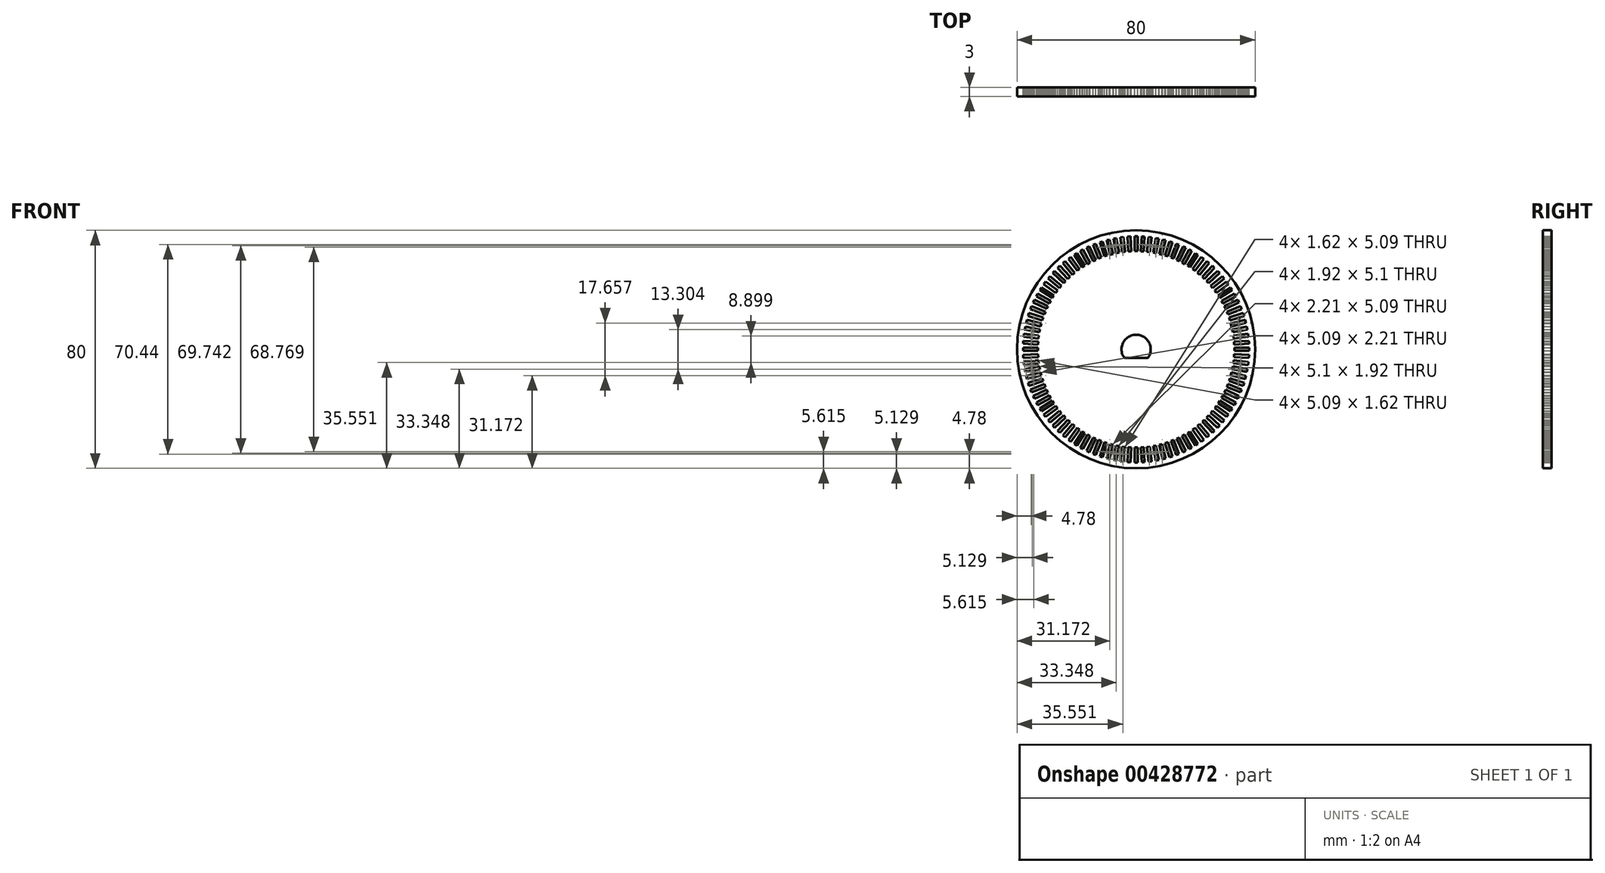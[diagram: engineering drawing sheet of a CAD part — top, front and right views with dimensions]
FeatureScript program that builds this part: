
annotation { "Feature Type Name" : "Feature", "Feature Type Description" : "" }
export const myFeature = defineFeature(function(context is Context, id is Id, definition is map)
    precondition{}
    {
        {
            var Q0;
            Q0=qCreatedBy(makeId("Front.planeOp"),FACE);
            var sketch = newSketch(context, id + "F0", { "sketchPlane" : qUnion([Q0])});
            skCircle(sketch, "E0", {"center": v(0, 0) * mm, "radius": 40 * mm});
            skLineSegment(sketch, "E1", {"start": v(0, 0) * mm, "end": v(0, 33) * mm});
            skLineSegment(sketch, "E2", {"start": v(0, 33) * mm, "end": v(0, 35.5) * mm});
            skLineSegment(sketch, "E3.bottom", {"start": v(0.5, 33) * mm, "end": v(-0.5, 33) * mm});
            skLineSegment(sketch, "E3.top", {"start": v(0.5, 38) * mm, "end": v(-0.5, 38) * mm});
            skLineSegment(sketch, "E3.left", {"start": v(0.5, 33) * mm, "end": v(0.5, 38) * mm});
            skLineSegment(sketch, "E3.right", {"start": v(-0.5, 33) * mm, "end": v(-0.5, 38) * mm});
            skPoint(sketch, "E3.middle", {"position": v(0, 35.5) * mm});
            skLineSegment(sketch, "E4.1.0", {"start": v(-2.57, 32.9) * mm, "end": v(-2.89, 37.9) * mm});
            skLineSegment(sketch, "E4.1.1", {"start": v(-1.57, 32.97) * mm, "end": v(-1.89, 37.96) * mm});
            skLineSegment(sketch, "E4.1.2", {"start": v(-2.07, 32.93) * mm, "end": v(-2.23, 35.43) * mm});
            skPoint(sketch, "E4.1.3", {"position": v(-2.23, 35.43) * mm});
            skLineSegment(sketch, "E4.1.4", {"start": v(-1.89, 37.96) * mm, "end": v(-2.89, 37.9) * mm});
            skLineSegment(sketch, "E4.1.5", {"start": v(-1.57, 32.97) * mm, "end": v(-2.57, 32.9) * mm});
            skLineSegment(sketch, "E4.2.0", {"start": v(-4.63, 32.68) * mm, "end": v(-5.26, 37.64) * mm});
            skLineSegment(sketch, "E4.2.1", {"start": v(-3.64, 32.8) * mm, "end": v(-4.27, 37.76) * mm});
            skLineSegment(sketch, "E4.2.2", {"start": v(-4.14, 32.74) * mm, "end": v(-4.45, 35.22) * mm});
            skPoint(sketch, "E4.2.3", {"position": v(-4.45, 35.22) * mm});
            skLineSegment(sketch, "E4.2.4", {"start": v(-4.27, 37.76) * mm, "end": v(-5.26, 37.64) * mm});
            skLineSegment(sketch, "E4.2.5", {"start": v(-3.64, 32.8) * mm, "end": v(-4.63, 32.68) * mm});
            skLineSegment(sketch, "E4.3.0", {"start": v(-6.67, 32.32) * mm, "end": v(-7.61, 37.23) * mm});
            skLineSegment(sketch, "E4.3.1", {"start": v(-5.7, 32.5) * mm, "end": v(-6.63, 37.42) * mm});
            skLineSegment(sketch, "E4.3.2", {"start": v(-6.18, 32.42) * mm, "end": v(-6.65, 34.87) * mm});
            skPoint(sketch, "E4.3.3", {"position": v(-6.65, 34.87) * mm});
            skLineSegment(sketch, "E4.3.4", {"start": v(-6.63, 37.42) * mm, "end": v(-7.61, 37.23) * mm});
            skLineSegment(sketch, "E4.3.5", {"start": v(-5.7, 32.5) * mm, "end": v(-6.67, 32.32) * mm});
            skLineSegment(sketch, "E4.4.0", {"start": v(-8.7, 31.84) * mm, "end": v(-9.93, 36.68) * mm});
            skLineSegment(sketch, "E4.4.1", {"start": v(-7.72, 32.09) * mm, "end": v(-8.97, 36.93) * mm});
            skLineSegment(sketch, "E4.4.2", {"start": v(-8.2, 31.96) * mm, "end": v(-8.83, 34.38) * mm});
            skPoint(sketch, "E4.4.3", {"position": v(-8.83, 34.38) * mm});
            skLineSegment(sketch, "E4.4.4", {"start": v(-8.97, 36.93) * mm, "end": v(-9.93, 36.68) * mm});
            skLineSegment(sketch, "E4.4.5", {"start": v(-7.72, 32.09) * mm, "end": v(-8.7, 31.84) * mm});
            skLineSegment(sketch, "E4.5.0", {"start": v(-10.67, 31.23) * mm, "end": v(-12.22, 35.99) * mm});
            skLineSegment(sketch, "E4.5.1", {"start": v(-9.72, 31.54) * mm, "end": v(-11.27, 36.3) * mm});
            skLineSegment(sketch, "E4.5.2", {"start": v(-10.2, 31.38) * mm, "end": v(-10.97, 33.76) * mm});
            skPoint(sketch, "E4.5.3", {"position": v(-10.97, 33.76) * mm});
            skLineSegment(sketch, "E4.5.4", {"start": v(-11.27, 36.3) * mm, "end": v(-12.22, 35.99) * mm});
            skLineSegment(sketch, "E4.5.5", {"start": v(-9.72, 31.54) * mm, "end": v(-10.67, 31.23) * mm});
            skLineSegment(sketch, "E4.6.0", {"start": v(-12.61, 30.5) * mm, "end": v(-14.45, 35.15) * mm});
            skLineSegment(sketch, "E4.6.1", {"start": v(-11.68, 30.87) * mm, "end": v(-13.52, 35.52) * mm});
            skLineSegment(sketch, "E4.6.2", {"start": v(-12.15, 30.68) * mm, "end": v(-13.07, 33) * mm});
            skPoint(sketch, "E4.6.3", {"position": v(-13.07, 33) * mm});
            skLineSegment(sketch, "E4.6.4", {"start": v(-13.52, 35.52) * mm, "end": v(-14.45, 35.15) * mm});
            skLineSegment(sketch, "E4.6.5", {"start": v(-11.68, 30.87) * mm, "end": v(-12.61, 30.5) * mm});
            skLineSegment(sketch, "E4.7.0", {"start": v(-14.5, 29.65) * mm, "end": v(-16.63, 34.17) * mm});
            skLineSegment(sketch, "E4.7.1", {"start": v(-13.6, 30.07) * mm, "end": v(-15.73, 34.6) * mm});
            skLineSegment(sketch, "E4.7.2", {"start": v(-14.05, 29.86) * mm, "end": v(-15.12, 32.12) * mm});
            skPoint(sketch, "E4.7.3", {"position": v(-15.12, 32.12) * mm});
            skLineSegment(sketch, "E4.7.4", {"start": v(-15.73, 34.6) * mm, "end": v(-16.63, 34.17) * mm});
            skLineSegment(sketch, "E4.7.5", {"start": v(-13.6, 30.07) * mm, "end": v(-14.5, 29.65) * mm});
            skLineSegment(sketch, "E4.8.0", {"start": v(-16.34, 28.68) * mm, "end": v(-18.74, 33.06) * mm});
            skLineSegment(sketch, "E4.8.1", {"start": v(-15.46, 29.16) * mm, "end": v(-17.87, 33.54) * mm});
            skLineSegment(sketch, "E4.8.2", {"start": v(-15.9, 28.92) * mm, "end": v(-17.1, 31.1) * mm});
            skPoint(sketch, "E4.8.3", {"position": v(-17.1, 31.1) * mm});
            skLineSegment(sketch, "E4.8.4", {"start": v(-17.87, 33.54) * mm, "end": v(-18.74, 33.06) * mm});
            skLineSegment(sketch, "E4.8.5", {"start": v(-15.46, 29.16) * mm, "end": v(-16.34, 28.68) * mm});
            skLineSegment(sketch, "E4.9.0", {"start": v(-18.1, 27.6) * mm, "end": v(-20.78, 31.82) * mm});
            skLineSegment(sketch, "E4.9.1", {"start": v(-17.26, 28.13) * mm, "end": v(-19.94, 32.35) * mm});
            skLineSegment(sketch, "E4.9.2", {"start": v(-17.68, 27.86) * mm, "end": v(-19.02, 29.97) * mm});
            skPoint(sketch, "E4.9.3", {"position": v(-19.02, 29.97) * mm});
            skLineSegment(sketch, "E4.9.4", {"start": v(-19.94, 32.35) * mm, "end": v(-20.78, 31.82) * mm});
            skLineSegment(sketch, "E4.9.5", {"start": v(-17.26, 28.13) * mm, "end": v(-18.1, 27.6) * mm});
            skLineSegment(sketch, "E4.10.0", {"start": v(-19.8, 26.4) * mm, "end": v(-22.74, 30.45) * mm});
            skLineSegment(sketch, "E4.10.1", {"start": v(-19, 27) * mm, "end": v(-21.93, 31.04) * mm});
            skLineSegment(sketch, "E4.10.2", {"start": v(-19.4, 26.7) * mm, "end": v(-20.87, 28.72) * mm});
            skPoint(sketch, "E4.10.3", {"position": v(-20.87, 28.72) * mm});
            skLineSegment(sketch, "E4.10.4", {"start": v(-21.93, 31.04) * mm, "end": v(-22.74, 30.45) * mm});
            skLineSegment(sketch, "E4.10.5", {"start": v(-19, 27) * mm, "end": v(-19.8, 26.4) * mm});
            skLineSegment(sketch, "E4.11.0", {"start": v(-21.42, 25.1) * mm, "end": v(-24.6, 28.96) * mm});
            skLineSegment(sketch, "E4.11.1", {"start": v(-20.65, 25.75) * mm, "end": v(-23.84, 29.6) * mm});
            skLineSegment(sketch, "E4.11.2", {"start": v(-21.03, 25.43) * mm, "end": v(-22.63, 27.35) * mm});
            skPoint(sketch, "E4.11.3", {"position": v(-22.63, 27.35) * mm});
            skLineSegment(sketch, "E4.11.4", {"start": v(-23.84, 29.6) * mm, "end": v(-24.6, 28.96) * mm});
            skLineSegment(sketch, "E4.11.5", {"start": v(-20.65, 25.75) * mm, "end": v(-21.42, 25.1) * mm});
            skLineSegment(sketch, "E4.12.0", {"start": v(-22.95, 23.71) * mm, "end": v(-26.38, 27.36) * mm});
            skLineSegment(sketch, "E4.12.1", {"start": v(-22.23, 24.4) * mm, "end": v(-25.65, 28.04) * mm});
            skLineSegment(sketch, "E4.12.2", {"start": v(-22.6, 24.06) * mm, "end": v(-24.3, 25.88) * mm});
            skPoint(sketch, "E4.12.3", {"position": v(-24.3, 25.88) * mm});
            skLineSegment(sketch, "E4.12.4", {"start": v(-25.65, 28.04) * mm, "end": v(-26.38, 27.36) * mm});
            skLineSegment(sketch, "E4.12.5", {"start": v(-22.23, 24.4) * mm, "end": v(-22.95, 23.71) * mm});
            skLineSegment(sketch, "E4.13.0", {"start": v(-24.4, 22.23) * mm, "end": v(-28.04, 25.65) * mm});
            skLineSegment(sketch, "E4.13.1", {"start": v(-23.71, 22.95) * mm, "end": v(-27.36, 26.38) * mm});
            skLineSegment(sketch, "E4.13.2", {"start": v(-24.06, 22.6) * mm, "end": v(-25.88, 24.3) * mm});
            skPoint(sketch, "E4.13.3", {"position": v(-25.88, 24.3) * mm});
            skLineSegment(sketch, "E4.13.4", {"start": v(-27.36, 26.38) * mm, "end": v(-28.04, 25.65) * mm});
            skLineSegment(sketch, "E4.13.5", {"start": v(-23.71, 22.95) * mm, "end": v(-24.4, 22.23) * mm});
            skLineSegment(sketch, "E4.14.0", {"start": v(-25.75, 20.65) * mm, "end": v(-29.6, 23.84) * mm});
            skLineSegment(sketch, "E4.14.1", {"start": v(-25.1, 21.42) * mm, "end": v(-28.96, 24.6) * mm});
            skLineSegment(sketch, "E4.14.2", {"start": v(-25.43, 21.03) * mm, "end": v(-27.35, 22.63) * mm});
            skPoint(sketch, "E4.14.3", {"position": v(-27.35, 22.63) * mm});
            skLineSegment(sketch, "E4.14.4", {"start": v(-28.96, 24.6) * mm, "end": v(-29.6, 23.84) * mm});
            skLineSegment(sketch, "E4.14.5", {"start": v(-25.1, 21.42) * mm, "end": v(-25.75, 20.65) * mm});
            skLineSegment(sketch, "E4.15.0", {"start": v(-27, 19) * mm, "end": v(-31.04, 21.93) * mm});
            skLineSegment(sketch, "E4.15.1", {"start": v(-26.4, 19.8) * mm, "end": v(-30.45, 22.74) * mm});
            skLineSegment(sketch, "E4.15.2", {"start": v(-26.7, 19.4) * mm, "end": v(-28.72, 20.87) * mm});
            skPoint(sketch, "E4.15.3", {"position": v(-28.72, 20.87) * mm});
            skLineSegment(sketch, "E4.15.4", {"start": v(-30.45, 22.74) * mm, "end": v(-31.04, 21.93) * mm});
            skLineSegment(sketch, "E4.15.5", {"start": v(-26.4, 19.8) * mm, "end": v(-27, 19) * mm});
            skLineSegment(sketch, "E4.16.0", {"start": v(-28.13, 17.26) * mm, "end": v(-32.35, 19.94) * mm});
            skLineSegment(sketch, "E4.16.1", {"start": v(-27.6, 18.1) * mm, "end": v(-31.82, 20.78) * mm});
            skLineSegment(sketch, "E4.16.2", {"start": v(-27.86, 17.68) * mm, "end": v(-29.97, 19.02) * mm});
            skPoint(sketch, "E4.16.3", {"position": v(-29.97, 19.02) * mm});
            skLineSegment(sketch, "E4.16.4", {"start": v(-31.82, 20.78) * mm, "end": v(-32.35, 19.94) * mm});
            skLineSegment(sketch, "E4.16.5", {"start": v(-27.6, 18.1) * mm, "end": v(-28.13, 17.26) * mm});
            skLineSegment(sketch, "E4.17.0", {"start": v(-29.16, 15.46) * mm, "end": v(-33.54, 17.87) * mm});
            skLineSegment(sketch, "E4.17.1", {"start": v(-28.68, 16.34) * mm, "end": v(-33.06, 18.74) * mm});
            skLineSegment(sketch, "E4.17.2", {"start": v(-28.92, 15.9) * mm, "end": v(-31.1, 17.1) * mm});
            skPoint(sketch, "E4.17.3", {"position": v(-31.1, 17.1) * mm});
            skLineSegment(sketch, "E4.17.4", {"start": v(-33.06, 18.74) * mm, "end": v(-33.54, 17.87) * mm});
            skLineSegment(sketch, "E4.17.5", {"start": v(-28.68, 16.34) * mm, "end": v(-29.16, 15.46) * mm});
            skLineSegment(sketch, "E4.18.0", {"start": v(-30.07, 13.6) * mm, "end": v(-34.6, 15.73) * mm});
            skLineSegment(sketch, "E4.18.1", {"start": v(-29.65, 14.5) * mm, "end": v(-34.17, 16.63) * mm});
            skLineSegment(sketch, "E4.18.2", {"start": v(-29.86, 14.05) * mm, "end": v(-32.12, 15.12) * mm});
            skPoint(sketch, "E4.18.3", {"position": v(-32.12, 15.12) * mm});
            skLineSegment(sketch, "E4.18.4", {"start": v(-34.17, 16.63) * mm, "end": v(-34.6, 15.73) * mm});
            skLineSegment(sketch, "E4.18.5", {"start": v(-29.65, 14.5) * mm, "end": v(-30.07, 13.6) * mm});
            skLineSegment(sketch, "E4.19.0", {"start": v(-30.87, 11.68) * mm, "end": v(-35.52, 13.52) * mm});
            skLineSegment(sketch, "E4.19.1", {"start": v(-30.5, 12.61) * mm, "end": v(-35.15, 14.45) * mm});
            skLineSegment(sketch, "E4.19.2", {"start": v(-30.68, 12.15) * mm, "end": v(-33, 13.07) * mm});
            skPoint(sketch, "E4.19.3", {"position": v(-33, 13.07) * mm});
            skLineSegment(sketch, "E4.19.4", {"start": v(-35.15, 14.45) * mm, "end": v(-35.52, 13.52) * mm});
            skLineSegment(sketch, "E4.19.5", {"start": v(-30.5, 12.61) * mm, "end": v(-30.87, 11.68) * mm});
            skLineSegment(sketch, "E5.1.20.0", {"start": v(-31.54, 9.72) * mm, "end": v(-36.3, 11.27) * mm});
            skLineSegment(sketch, "E5.3.20.0", {"start": v(-31.23, 10.67) * mm, "end": v(-35.99, 12.22) * mm});
            skLineSegment(sketch, "E5.6.20.0", {"start": v(-31.38, 10.2) * mm, "end": v(-33.76, 10.97) * mm});
            skPoint(sketch, "E5.9.20.0", {"position": v(-33.76, 10.97) * mm});
            skLineSegment(sketch, "E5.10.20.0", {"start": v(-35.99, 12.22) * mm, "end": v(-36.3, 11.27) * mm});
            skLineSegment(sketch, "E5.13.20.0", {"start": v(-31.23, 10.67) * mm, "end": v(-31.54, 9.72) * mm});
            skLineSegment(sketch, "E5.1.21.0", {"start": v(-32.09, 7.72) * mm, "end": v(-36.93, 8.97) * mm});
            skLineSegment(sketch, "E5.3.21.0", {"start": v(-31.84, 8.7) * mm, "end": v(-36.68, 9.93) * mm});
            skLineSegment(sketch, "E5.6.21.0", {"start": v(-31.96, 8.2) * mm, "end": v(-34.38, 8.83) * mm});
            skPoint(sketch, "E5.9.21.0", {"position": v(-34.38, 8.83) * mm});
            skLineSegment(sketch, "E5.10.21.0", {"start": v(-36.68, 9.93) * mm, "end": v(-36.93, 8.97) * mm});
            skLineSegment(sketch, "E5.13.21.0", {"start": v(-31.84, 8.7) * mm, "end": v(-32.09, 7.72) * mm});
            skLineSegment(sketch, "E5.1.22.0", {"start": v(-32.5, 5.7) * mm, "end": v(-37.42, 6.63) * mm});
            skLineSegment(sketch, "E5.3.22.0", {"start": v(-32.32, 6.67) * mm, "end": v(-37.23, 7.61) * mm});
            skLineSegment(sketch, "E5.6.22.0", {"start": v(-32.42, 6.18) * mm, "end": v(-34.87, 6.65) * mm});
            skPoint(sketch, "E5.9.22.0", {"position": v(-34.87, 6.65) * mm});
            skLineSegment(sketch, "E5.10.22.0", {"start": v(-37.23, 7.61) * mm, "end": v(-37.42, 6.63) * mm});
            skLineSegment(sketch, "E5.13.22.0", {"start": v(-32.32, 6.67) * mm, "end": v(-32.5, 5.7) * mm});
            skLineSegment(sketch, "E5.1.23.0", {"start": v(-32.8, 3.64) * mm, "end": v(-37.76, 4.27) * mm});
            skLineSegment(sketch, "E5.3.23.0", {"start": v(-32.68, 4.63) * mm, "end": v(-37.64, 5.26) * mm});
            skLineSegment(sketch, "E5.6.23.0", {"start": v(-32.74, 4.14) * mm, "end": v(-35.22, 4.45) * mm});
            skPoint(sketch, "E5.9.23.0", {"position": v(-35.22, 4.45) * mm});
            skLineSegment(sketch, "E5.10.23.0", {"start": v(-37.64, 5.26) * mm, "end": v(-37.76, 4.27) * mm});
            skLineSegment(sketch, "E5.13.23.0", {"start": v(-32.68, 4.63) * mm, "end": v(-32.8, 3.64) * mm});
            skLineSegment(sketch, "E5.1.24.0", {"start": v(-32.97, 1.57) * mm, "end": v(-37.96, 1.89) * mm});
            skLineSegment(sketch, "E5.3.24.0", {"start": v(-32.9, 2.57) * mm, "end": v(-37.9, 2.89) * mm});
            skLineSegment(sketch, "E5.6.24.0", {"start": v(-32.93, 2.07) * mm, "end": v(-35.43, 2.23) * mm});
            skPoint(sketch, "E5.9.24.0", {"position": v(-35.43, 2.23) * mm});
            skLineSegment(sketch, "E5.10.24.0", {"start": v(-37.9, 2.89) * mm, "end": v(-37.96, 1.89) * mm});
            skLineSegment(sketch, "E5.13.24.0", {"start": v(-32.9, 2.57) * mm, "end": v(-32.97, 1.57) * mm});
            skLineSegment(sketch, "E5.1.25.0", {"start": v(-33, -0.5) * mm, "end": v(-38, -0.5) * mm});
            skLineSegment(sketch, "E5.3.25.0", {"start": v(-33, 0.5) * mm, "end": v(-38, 0.5) * mm});
            skLineSegment(sketch, "E5.6.25.0", {"start": v(-33, 0) * mm, "end": v(-35.5, 0) * mm});
            skPoint(sketch, "E5.9.25.0", {"position": v(-35.5, 0) * mm});
            skLineSegment(sketch, "E5.10.25.0", {"start": v(-38, 0.5) * mm, "end": v(-38, -0.5) * mm});
            skLineSegment(sketch, "E5.13.25.0", {"start": v(-33, 0.5) * mm, "end": v(-33, -0.5) * mm});
            skLineSegment(sketch, "E5.1.26.0", {"start": v(-32.9, -2.57) * mm, "end": v(-37.9, -2.89) * mm});
            skLineSegment(sketch, "E5.3.26.0", {"start": v(-32.97, -1.57) * mm, "end": v(-37.96, -1.89) * mm});
            skLineSegment(sketch, "E5.6.26.0", {"start": v(-32.93, -2.07) * mm, "end": v(-35.43, -2.23) * mm});
            skPoint(sketch, "E5.9.26.0", {"position": v(-35.43, -2.23) * mm});
            skLineSegment(sketch, "E5.10.26.0", {"start": v(-37.96, -1.89) * mm, "end": v(-37.9, -2.89) * mm});
            skLineSegment(sketch, "E5.13.26.0", {"start": v(-32.97, -1.57) * mm, "end": v(-32.9, -2.57) * mm});
            skLineSegment(sketch, "E5.1.27.0", {"start": v(-32.68, -4.63) * mm, "end": v(-37.64, -5.26) * mm});
            skLineSegment(sketch, "E5.3.27.0", {"start": v(-32.8, -3.64) * mm, "end": v(-37.76, -4.27) * mm});
            skLineSegment(sketch, "E5.6.27.0", {"start": v(-32.74, -4.14) * mm, "end": v(-35.22, -4.45) * mm});
            skPoint(sketch, "E5.9.27.0", {"position": v(-35.22, -4.45) * mm});
            skLineSegment(sketch, "E5.10.27.0", {"start": v(-37.76, -4.27) * mm, "end": v(-37.64, -5.26) * mm});
            skLineSegment(sketch, "E5.13.27.0", {"start": v(-32.8, -3.64) * mm, "end": v(-32.68, -4.63) * mm});
            skLineSegment(sketch, "E5.1.28.0", {"start": v(-32.32, -6.67) * mm, "end": v(-37.23, -7.61) * mm});
            skLineSegment(sketch, "E5.3.28.0", {"start": v(-32.5, -5.7) * mm, "end": v(-37.42, -6.63) * mm});
            skLineSegment(sketch, "E5.6.28.0", {"start": v(-32.42, -6.18) * mm, "end": v(-34.87, -6.65) * mm});
            skPoint(sketch, "E5.9.28.0", {"position": v(-34.87, -6.65) * mm});
            skLineSegment(sketch, "E5.10.28.0", {"start": v(-37.42, -6.63) * mm, "end": v(-37.23, -7.61) * mm});
            skLineSegment(sketch, "E5.13.28.0", {"start": v(-32.5, -5.7) * mm, "end": v(-32.32, -6.67) * mm});
            skLineSegment(sketch, "E5.1.29.0", {"start": v(-31.84, -8.7) * mm, "end": v(-36.68, -9.93) * mm});
            skLineSegment(sketch, "E5.3.29.0", {"start": v(-32.09, -7.72) * mm, "end": v(-36.93, -8.97) * mm});
            skLineSegment(sketch, "E5.6.29.0", {"start": v(-31.96, -8.2) * mm, "end": v(-34.38, -8.83) * mm});
            skPoint(sketch, "E5.9.29.0", {"position": v(-34.38, -8.83) * mm});
            skLineSegment(sketch, "E5.10.29.0", {"start": v(-36.93, -8.97) * mm, "end": v(-36.68, -9.93) * mm});
            skLineSegment(sketch, "E5.13.29.0", {"start": v(-32.09, -7.72) * mm, "end": v(-31.84, -8.7) * mm});
            skLineSegment(sketch, "E5.1.30.0", {"start": v(-31.23, -10.67) * mm, "end": v(-35.99, -12.22) * mm});
            skLineSegment(sketch, "E5.3.30.0", {"start": v(-31.54, -9.72) * mm, "end": v(-36.3, -11.27) * mm});
            skLineSegment(sketch, "E5.6.30.0", {"start": v(-31.38, -10.2) * mm, "end": v(-33.76, -10.97) * mm});
            skPoint(sketch, "E5.9.30.0", {"position": v(-33.76, -10.97) * mm});
            skLineSegment(sketch, "E5.10.30.0", {"start": v(-36.3, -11.27) * mm, "end": v(-35.99, -12.22) * mm});
            skLineSegment(sketch, "E5.13.30.0", {"start": v(-31.54, -9.72) * mm, "end": v(-31.23, -10.67) * mm});
            skLineSegment(sketch, "E5.1.31.0", {"start": v(-30.5, -12.61) * mm, "end": v(-35.15, -14.45) * mm});
            skLineSegment(sketch, "E5.3.31.0", {"start": v(-30.87, -11.68) * mm, "end": v(-35.52, -13.52) * mm});
            skLineSegment(sketch, "E5.6.31.0", {"start": v(-30.68, -12.15) * mm, "end": v(-33, -13.07) * mm});
            skPoint(sketch, "E5.9.31.0", {"position": v(-33, -13.07) * mm});
            skLineSegment(sketch, "E5.10.31.0", {"start": v(-35.52, -13.52) * mm, "end": v(-35.15, -14.45) * mm});
            skLineSegment(sketch, "E5.13.31.0", {"start": v(-30.87, -11.68) * mm, "end": v(-30.5, -12.61) * mm});
            skLineSegment(sketch, "E5.1.32.0", {"start": v(-29.65, -14.5) * mm, "end": v(-34.17, -16.63) * mm});
            skLineSegment(sketch, "E5.3.32.0", {"start": v(-30.07, -13.6) * mm, "end": v(-34.6, -15.73) * mm});
            skLineSegment(sketch, "E5.6.32.0", {"start": v(-29.86, -14.05) * mm, "end": v(-32.12, -15.12) * mm});
            skPoint(sketch, "E5.9.32.0", {"position": v(-32.12, -15.12) * mm});
            skLineSegment(sketch, "E5.10.32.0", {"start": v(-34.6, -15.73) * mm, "end": v(-34.17, -16.63) * mm});
            skLineSegment(sketch, "E5.13.32.0", {"start": v(-30.07, -13.6) * mm, "end": v(-29.65, -14.5) * mm});
            skLineSegment(sketch, "E5.1.33.0", {"start": v(-28.68, -16.34) * mm, "end": v(-33.06, -18.74) * mm});
            skLineSegment(sketch, "E5.3.33.0", {"start": v(-29.16, -15.46) * mm, "end": v(-33.54, -17.87) * mm});
            skLineSegment(sketch, "E5.6.33.0", {"start": v(-28.92, -15.9) * mm, "end": v(-31.1, -17.1) * mm});
            skPoint(sketch, "E5.9.33.0", {"position": v(-31.1, -17.1) * mm});
            skLineSegment(sketch, "E5.10.33.0", {"start": v(-33.54, -17.87) * mm, "end": v(-33.06, -18.74) * mm});
            skLineSegment(sketch, "E5.13.33.0", {"start": v(-29.16, -15.46) * mm, "end": v(-28.68, -16.34) * mm});
            skLineSegment(sketch, "E5.1.34.0", {"start": v(-27.6, -18.1) * mm, "end": v(-31.82, -20.78) * mm});
            skLineSegment(sketch, "E5.3.34.0", {"start": v(-28.13, -17.26) * mm, "end": v(-32.35, -19.94) * mm});
            skLineSegment(sketch, "E5.6.34.0", {"start": v(-27.86, -17.68) * mm, "end": v(-29.97, -19.02) * mm});
            skPoint(sketch, "E5.9.34.0", {"position": v(-29.97, -19.02) * mm});
            skLineSegment(sketch, "E5.10.34.0", {"start": v(-32.35, -19.94) * mm, "end": v(-31.82, -20.78) * mm});
            skLineSegment(sketch, "E5.13.34.0", {"start": v(-28.13, -17.26) * mm, "end": v(-27.6, -18.1) * mm});
            skLineSegment(sketch, "E5.1.35.0", {"start": v(-26.4, -19.8) * mm, "end": v(-30.45, -22.74) * mm});
            skLineSegment(sketch, "E5.3.35.0", {"start": v(-27, -19) * mm, "end": v(-31.04, -21.93) * mm});
            skLineSegment(sketch, "E5.6.35.0", {"start": v(-26.7, -19.4) * mm, "end": v(-28.72, -20.87) * mm});
            skPoint(sketch, "E5.9.35.0", {"position": v(-28.72, -20.87) * mm});
            skLineSegment(sketch, "E5.10.35.0", {"start": v(-31.04, -21.93) * mm, "end": v(-30.45, -22.74) * mm});
            skLineSegment(sketch, "E5.13.35.0", {"start": v(-27, -19) * mm, "end": v(-26.4, -19.8) * mm});
            skLineSegment(sketch, "E5.1.36.0", {"start": v(-25.1, -21.42) * mm, "end": v(-28.96, -24.6) * mm});
            skLineSegment(sketch, "E5.3.36.0", {"start": v(-25.75, -20.65) * mm, "end": v(-29.6, -23.84) * mm});
            skLineSegment(sketch, "E5.6.36.0", {"start": v(-25.43, -21.03) * mm, "end": v(-27.35, -22.63) * mm});
            skPoint(sketch, "E5.9.36.0", {"position": v(-27.35, -22.63) * mm});
            skLineSegment(sketch, "E5.10.36.0", {"start": v(-29.6, -23.84) * mm, "end": v(-28.96, -24.6) * mm});
            skLineSegment(sketch, "E5.13.36.0", {"start": v(-25.75, -20.65) * mm, "end": v(-25.1, -21.42) * mm});
            skLineSegment(sketch, "E5.1.37.0", {"start": v(-23.71, -22.95) * mm, "end": v(-27.36, -26.38) * mm});
            skLineSegment(sketch, "E5.3.37.0", {"start": v(-24.4, -22.23) * mm, "end": v(-28.04, -25.65) * mm});
            skLineSegment(sketch, "E5.6.37.0", {"start": v(-24.06, -22.6) * mm, "end": v(-25.88, -24.3) * mm});
            skPoint(sketch, "E5.9.37.0", {"position": v(-25.88, -24.3) * mm});
            skLineSegment(sketch, "E5.10.37.0", {"start": v(-28.04, -25.65) * mm, "end": v(-27.36, -26.38) * mm});
            skLineSegment(sketch, "E5.13.37.0", {"start": v(-24.4, -22.23) * mm, "end": v(-23.71, -22.95) * mm});
            skLineSegment(sketch, "E5.1.38.0", {"start": v(-22.23, -24.4) * mm, "end": v(-25.65, -28.04) * mm});
            skLineSegment(sketch, "E5.3.38.0", {"start": v(-22.95, -23.71) * mm, "end": v(-26.38, -27.36) * mm});
            skLineSegment(sketch, "E5.6.38.0", {"start": v(-22.6, -24.06) * mm, "end": v(-24.3, -25.88) * mm});
            skPoint(sketch, "E5.9.38.0", {"position": v(-24.3, -25.88) * mm});
            skLineSegment(sketch, "E5.10.38.0", {"start": v(-26.38, -27.36) * mm, "end": v(-25.65, -28.04) * mm});
            skLineSegment(sketch, "E5.13.38.0", {"start": v(-22.95, -23.71) * mm, "end": v(-22.23, -24.4) * mm});
            skLineSegment(sketch, "E5.1.39.0", {"start": v(-20.65, -25.75) * mm, "end": v(-23.84, -29.6) * mm});
            skLineSegment(sketch, "E5.3.39.0", {"start": v(-21.42, -25.1) * mm, "end": v(-24.6, -28.96) * mm});
            skLineSegment(sketch, "E5.6.39.0", {"start": v(-21.03, -25.43) * mm, "end": v(-22.63, -27.35) * mm});
            skPoint(sketch, "E5.9.39.0", {"position": v(-22.63, -27.35) * mm});
            skLineSegment(sketch, "E5.10.39.0", {"start": v(-24.6, -28.96) * mm, "end": v(-23.84, -29.6) * mm});
            skLineSegment(sketch, "E5.13.39.0", {"start": v(-21.42, -25.1) * mm, "end": v(-20.65, -25.75) * mm});
            skArc(sketch, "E6", {"start": v(3.95, -2.9) * mm, "mid": v(0, 4.9) * mm, "end": v(-3.95, -2.9) * mm});
            skLineSegment(sketch, "E7", {"start": v(0, 4.9) * mm, "end": v(0, -2.9) * mm, "construction": true});
            skLineSegment(sketch, "E8", {"start": v(-3.95, -2.9) * mm, "end": v(3.95, -2.9) * mm});
            skLineSegment(sketch, "E9.1.40.0", {"start": v(-19, -27) * mm, "end": v(-21.93, -31.04) * mm});
            skLineSegment(sketch, "E9.3.40.0", {"start": v(-19.8, -26.4) * mm, "end": v(-22.74, -30.45) * mm});
            skLineSegment(sketch, "E9.6.40.0", {"start": v(-19.4, -26.7) * mm, "end": v(-20.87, -28.72) * mm});
            skPoint(sketch, "E9.9.40.0", {"position": v(-20.87, -28.72) * mm});
            skLineSegment(sketch, "E9.10.40.0", {"start": v(-22.74, -30.45) * mm, "end": v(-21.93, -31.04) * mm});
            skLineSegment(sketch, "E9.13.40.0", {"start": v(-19.8, -26.4) * mm, "end": v(-19, -27) * mm});
            skLineSegment(sketch, "E9.1.41.0", {"start": v(-17.26, -28.13) * mm, "end": v(-19.94, -32.35) * mm});
            skLineSegment(sketch, "E9.3.41.0", {"start": v(-18.1, -27.6) * mm, "end": v(-20.78, -31.82) * mm});
            skLineSegment(sketch, "E9.6.41.0", {"start": v(-17.68, -27.86) * mm, "end": v(-19.02, -29.97) * mm});
            skPoint(sketch, "E9.9.41.0", {"position": v(-19.02, -29.97) * mm});
            skLineSegment(sketch, "E9.10.41.0", {"start": v(-20.78, -31.82) * mm, "end": v(-19.94, -32.35) * mm});
            skLineSegment(sketch, "E9.13.41.0", {"start": v(-18.1, -27.6) * mm, "end": v(-17.26, -28.13) * mm});
            skLineSegment(sketch, "E9.1.42.0", {"start": v(-15.46, -29.16) * mm, "end": v(-17.87, -33.54) * mm});
            skLineSegment(sketch, "E9.3.42.0", {"start": v(-16.34, -28.68) * mm, "end": v(-18.74, -33.06) * mm});
            skLineSegment(sketch, "E9.6.42.0", {"start": v(-15.9, -28.92) * mm, "end": v(-17.1, -31.1) * mm});
            skPoint(sketch, "E9.9.42.0", {"position": v(-17.1, -31.1) * mm});
            skLineSegment(sketch, "E9.10.42.0", {"start": v(-18.74, -33.06) * mm, "end": v(-17.87, -33.54) * mm});
            skLineSegment(sketch, "E9.13.42.0", {"start": v(-16.34, -28.68) * mm, "end": v(-15.46, -29.16) * mm});
            skLineSegment(sketch, "E9.1.43.0", {"start": v(-13.6, -30.07) * mm, "end": v(-15.73, -34.6) * mm});
            skLineSegment(sketch, "E9.3.43.0", {"start": v(-14.5, -29.65) * mm, "end": v(-16.63, -34.17) * mm});
            skLineSegment(sketch, "E9.6.43.0", {"start": v(-14.05, -29.86) * mm, "end": v(-15.12, -32.12) * mm});
            skPoint(sketch, "E9.9.43.0", {"position": v(-15.12, -32.12) * mm});
            skLineSegment(sketch, "E9.10.43.0", {"start": v(-16.63, -34.17) * mm, "end": v(-15.73, -34.6) * mm});
            skLineSegment(sketch, "E9.13.43.0", {"start": v(-14.5, -29.65) * mm, "end": v(-13.6, -30.07) * mm});
            skLineSegment(sketch, "E9.1.44.0", {"start": v(-11.68, -30.87) * mm, "end": v(-13.52, -35.52) * mm});
            skLineSegment(sketch, "E9.3.44.0", {"start": v(-12.61, -30.5) * mm, "end": v(-14.45, -35.15) * mm});
            skLineSegment(sketch, "E9.6.44.0", {"start": v(-12.15, -30.68) * mm, "end": v(-13.07, -33) * mm});
            skPoint(sketch, "E9.9.44.0", {"position": v(-13.07, -33) * mm});
            skLineSegment(sketch, "E9.10.44.0", {"start": v(-14.45, -35.15) * mm, "end": v(-13.52, -35.52) * mm});
            skLineSegment(sketch, "E9.13.44.0", {"start": v(-12.61, -30.5) * mm, "end": v(-11.68, -30.87) * mm});
            skLineSegment(sketch, "E9.1.45.0", {"start": v(-9.72, -31.54) * mm, "end": v(-11.27, -36.3) * mm});
            skLineSegment(sketch, "E9.3.45.0", {"start": v(-10.67, -31.23) * mm, "end": v(-12.22, -35.99) * mm});
            skLineSegment(sketch, "E9.6.45.0", {"start": v(-10.2, -31.38) * mm, "end": v(-10.97, -33.76) * mm});
            skPoint(sketch, "E9.9.45.0", {"position": v(-10.97, -33.76) * mm});
            skLineSegment(sketch, "E9.10.45.0", {"start": v(-12.22, -35.99) * mm, "end": v(-11.27, -36.3) * mm});
            skLineSegment(sketch, "E9.13.45.0", {"start": v(-10.67, -31.23) * mm, "end": v(-9.72, -31.54) * mm});
            skLineSegment(sketch, "E9.1.46.0", {"start": v(-7.72, -32.09) * mm, "end": v(-8.97, -36.93) * mm});
            skLineSegment(sketch, "E9.3.46.0", {"start": v(-8.7, -31.84) * mm, "end": v(-9.93, -36.68) * mm});
            skLineSegment(sketch, "E9.6.46.0", {"start": v(-8.2, -31.96) * mm, "end": v(-8.83, -34.38) * mm});
            skPoint(sketch, "E9.9.46.0", {"position": v(-8.83, -34.38) * mm});
            skLineSegment(sketch, "E9.10.46.0", {"start": v(-9.93, -36.68) * mm, "end": v(-8.97, -36.93) * mm});
            skLineSegment(sketch, "E9.13.46.0", {"start": v(-8.7, -31.84) * mm, "end": v(-7.72, -32.09) * mm});
            skLineSegment(sketch, "E9.1.47.0", {"start": v(-5.7, -32.5) * mm, "end": v(-6.63, -37.42) * mm});
            skLineSegment(sketch, "E9.3.47.0", {"start": v(-6.67, -32.32) * mm, "end": v(-7.61, -37.23) * mm});
            skLineSegment(sketch, "E9.6.47.0", {"start": v(-6.18, -32.42) * mm, "end": v(-6.65, -34.87) * mm});
            skPoint(sketch, "E9.9.47.0", {"position": v(-6.65, -34.87) * mm});
            skLineSegment(sketch, "E9.10.47.0", {"start": v(-7.61, -37.23) * mm, "end": v(-6.63, -37.42) * mm});
            skLineSegment(sketch, "E9.13.47.0", {"start": v(-6.67, -32.32) * mm, "end": v(-5.7, -32.5) * mm});
            skLineSegment(sketch, "E9.1.48.0", {"start": v(-3.64, -32.8) * mm, "end": v(-4.27, -37.76) * mm});
            skLineSegment(sketch, "E9.3.48.0", {"start": v(-4.63, -32.68) * mm, "end": v(-5.26, -37.64) * mm});
            skLineSegment(sketch, "E9.6.48.0", {"start": v(-4.14, -32.74) * mm, "end": v(-4.45, -35.22) * mm});
            skPoint(sketch, "E9.9.48.0", {"position": v(-4.45, -35.22) * mm});
            skLineSegment(sketch, "E9.10.48.0", {"start": v(-5.26, -37.64) * mm, "end": v(-4.27, -37.76) * mm});
            skLineSegment(sketch, "E9.13.48.0", {"start": v(-4.63, -32.68) * mm, "end": v(-3.64, -32.8) * mm});
            skLineSegment(sketch, "E9.1.49.0", {"start": v(-1.57, -32.97) * mm, "end": v(-1.89, -37.96) * mm});
            skLineSegment(sketch, "E9.3.49.0", {"start": v(-2.57, -32.9) * mm, "end": v(-2.89, -37.9) * mm});
            skLineSegment(sketch, "E9.6.49.0", {"start": v(-2.07, -32.93) * mm, "end": v(-2.23, -35.43) * mm});
            skPoint(sketch, "E9.9.49.0", {"position": v(-2.23, -35.43) * mm});
            skLineSegment(sketch, "E9.10.49.0", {"start": v(-2.89, -37.9) * mm, "end": v(-1.89, -37.96) * mm});
            skLineSegment(sketch, "E9.13.49.0", {"start": v(-2.57, -32.9) * mm, "end": v(-1.57, -32.97) * mm});
            skLineSegment(sketch, "E9.1.50.0", {"start": v(0.5, -33) * mm, "end": v(0.5, -38) * mm});
            skLineSegment(sketch, "E9.3.50.0", {"start": v(-0.5, -33) * mm, "end": v(-0.5, -38) * mm});
            skLineSegment(sketch, "E9.6.50.0", {"start": v(0, -33) * mm, "end": v(0, -35.5) * mm});
            skPoint(sketch, "E9.9.50.0", {"position": v(0, -35.5) * mm});
            skLineSegment(sketch, "E9.10.50.0", {"start": v(-0.5, -38) * mm, "end": v(0.5, -38) * mm});
            skLineSegment(sketch, "E9.13.50.0", {"start": v(-0.5, -33) * mm, "end": v(0.5, -33) * mm});
            skLineSegment(sketch, "E9.1.51.0", {"start": v(2.57, -32.9) * mm, "end": v(2.89, -37.9) * mm});
            skLineSegment(sketch, "E9.3.51.0", {"start": v(1.57, -32.97) * mm, "end": v(1.89, -37.96) * mm});
            skLineSegment(sketch, "E9.6.51.0", {"start": v(2.07, -32.93) * mm, "end": v(2.23, -35.43) * mm});
            skPoint(sketch, "E9.9.51.0", {"position": v(2.23, -35.43) * mm});
            skLineSegment(sketch, "E9.10.51.0", {"start": v(1.89, -37.96) * mm, "end": v(2.89, -37.9) * mm});
            skLineSegment(sketch, "E9.13.51.0", {"start": v(1.57, -32.97) * mm, "end": v(2.57, -32.9) * mm});
            skLineSegment(sketch, "E9.1.52.0", {"start": v(4.63, -32.68) * mm, "end": v(5.26, -37.64) * mm});
            skLineSegment(sketch, "E9.3.52.0", {"start": v(3.64, -32.8) * mm, "end": v(4.27, -37.76) * mm});
            skLineSegment(sketch, "E9.6.52.0", {"start": v(4.14, -32.74) * mm, "end": v(4.45, -35.22) * mm});
            skPoint(sketch, "E9.9.52.0", {"position": v(4.45, -35.22) * mm});
            skLineSegment(sketch, "E9.10.52.0", {"start": v(4.27, -37.76) * mm, "end": v(5.26, -37.64) * mm});
            skLineSegment(sketch, "E9.13.52.0", {"start": v(3.64, -32.8) * mm, "end": v(4.63, -32.68) * mm});
            skLineSegment(sketch, "E9.1.53.0", {"start": v(6.67, -32.32) * mm, "end": v(7.61, -37.23) * mm});
            skLineSegment(sketch, "E9.3.53.0", {"start": v(5.7, -32.5) * mm, "end": v(6.63, -37.42) * mm});
            skLineSegment(sketch, "E9.6.53.0", {"start": v(6.18, -32.42) * mm, "end": v(6.65, -34.87) * mm});
            skPoint(sketch, "E9.9.53.0", {"position": v(6.65, -34.87) * mm});
            skLineSegment(sketch, "E9.10.53.0", {"start": v(6.63, -37.42) * mm, "end": v(7.61, -37.23) * mm});
            skLineSegment(sketch, "E9.13.53.0", {"start": v(5.7, -32.5) * mm, "end": v(6.67, -32.32) * mm});
            skLineSegment(sketch, "E9.1.54.0", {"start": v(8.7, -31.84) * mm, "end": v(9.93, -36.68) * mm});
            skLineSegment(sketch, "E9.3.54.0", {"start": v(7.72, -32.09) * mm, "end": v(8.97, -36.93) * mm});
            skLineSegment(sketch, "E9.6.54.0", {"start": v(8.2, -31.96) * mm, "end": v(8.83, -34.38) * mm});
            skPoint(sketch, "E9.9.54.0", {"position": v(8.83, -34.38) * mm});
            skLineSegment(sketch, "E9.10.54.0", {"start": v(8.97, -36.93) * mm, "end": v(9.93, -36.68) * mm});
            skLineSegment(sketch, "E9.13.54.0", {"start": v(7.72, -32.09) * mm, "end": v(8.7, -31.84) * mm});
            skLineSegment(sketch, "E9.1.55.0", {"start": v(10.67, -31.23) * mm, "end": v(12.22, -35.99) * mm});
            skLineSegment(sketch, "E9.3.55.0", {"start": v(9.72, -31.54) * mm, "end": v(11.27, -36.3) * mm});
            skLineSegment(sketch, "E9.6.55.0", {"start": v(10.2, -31.38) * mm, "end": v(10.97, -33.76) * mm});
            skPoint(sketch, "E9.9.55.0", {"position": v(10.97, -33.76) * mm});
            skLineSegment(sketch, "E9.10.55.0", {"start": v(11.27, -36.3) * mm, "end": v(12.22, -35.99) * mm});
            skLineSegment(sketch, "E9.13.55.0", {"start": v(9.72, -31.54) * mm, "end": v(10.67, -31.23) * mm});
            skLineSegment(sketch, "E9.1.56.0", {"start": v(12.61, -30.5) * mm, "end": v(14.45, -35.15) * mm});
            skLineSegment(sketch, "E9.3.56.0", {"start": v(11.68, -30.87) * mm, "end": v(13.52, -35.52) * mm});
            skLineSegment(sketch, "E9.6.56.0", {"start": v(12.15, -30.68) * mm, "end": v(13.07, -33) * mm});
            skPoint(sketch, "E9.9.56.0", {"position": v(13.07, -33) * mm});
            skLineSegment(sketch, "E9.10.56.0", {"start": v(13.52, -35.52) * mm, "end": v(14.45, -35.15) * mm});
            skLineSegment(sketch, "E9.13.56.0", {"start": v(11.68, -30.87) * mm, "end": v(12.61, -30.5) * mm});
            skLineSegment(sketch, "E9.1.57.0", {"start": v(14.5, -29.65) * mm, "end": v(16.63, -34.17) * mm});
            skLineSegment(sketch, "E9.3.57.0", {"start": v(13.6, -30.07) * mm, "end": v(15.73, -34.6) * mm});
            skLineSegment(sketch, "E9.6.57.0", {"start": v(14.05, -29.86) * mm, "end": v(15.12, -32.12) * mm});
            skPoint(sketch, "E9.9.57.0", {"position": v(15.12, -32.12) * mm});
            skLineSegment(sketch, "E9.10.57.0", {"start": v(15.73, -34.6) * mm, "end": v(16.63, -34.17) * mm});
            skLineSegment(sketch, "E9.13.57.0", {"start": v(13.6, -30.07) * mm, "end": v(14.5, -29.65) * mm});
            skLineSegment(sketch, "E9.1.58.0", {"start": v(16.34, -28.68) * mm, "end": v(18.74, -33.06) * mm});
            skLineSegment(sketch, "E9.3.58.0", {"start": v(15.46, -29.16) * mm, "end": v(17.87, -33.54) * mm});
            skLineSegment(sketch, "E9.6.58.0", {"start": v(15.9, -28.92) * mm, "end": v(17.1, -31.1) * mm});
            skPoint(sketch, "E9.9.58.0", {"position": v(17.1, -31.1) * mm});
            skLineSegment(sketch, "E9.10.58.0", {"start": v(17.87, -33.54) * mm, "end": v(18.74, -33.06) * mm});
            skLineSegment(sketch, "E9.13.58.0", {"start": v(15.46, -29.16) * mm, "end": v(16.34, -28.68) * mm});
            skLineSegment(sketch, "E9.1.59.0", {"start": v(18.1, -27.6) * mm, "end": v(20.78, -31.82) * mm});
            skLineSegment(sketch, "E9.3.59.0", {"start": v(17.26, -28.13) * mm, "end": v(19.94, -32.35) * mm});
            skLineSegment(sketch, "E9.6.59.0", {"start": v(17.68, -27.86) * mm, "end": v(19.02, -29.97) * mm});
            skPoint(sketch, "E9.9.59.0", {"position": v(19.02, -29.97) * mm});
            skLineSegment(sketch, "E9.10.59.0", {"start": v(19.94, -32.35) * mm, "end": v(20.78, -31.82) * mm});
            skLineSegment(sketch, "E9.13.59.0", {"start": v(17.26, -28.13) * mm, "end": v(18.1, -27.6) * mm});
            skLineSegment(sketch, "E9.1.60.0", {"start": v(19.8, -26.4) * mm, "end": v(22.74, -30.45) * mm});
            skLineSegment(sketch, "E9.3.60.0", {"start": v(19, -27) * mm, "end": v(21.93, -31.04) * mm});
            skLineSegment(sketch, "E9.6.60.0", {"start": v(19.4, -26.7) * mm, "end": v(20.87, -28.72) * mm});
            skPoint(sketch, "E9.9.60.0", {"position": v(20.87, -28.72) * mm});
            skLineSegment(sketch, "E9.10.60.0", {"start": v(21.93, -31.04) * mm, "end": v(22.74, -30.45) * mm});
            skLineSegment(sketch, "E9.13.60.0", {"start": v(19, -27) * mm, "end": v(19.8, -26.4) * mm});
            skLineSegment(sketch, "E9.1.61.0", {"start": v(21.42, -25.1) * mm, "end": v(24.6, -28.96) * mm});
            skLineSegment(sketch, "E9.3.61.0", {"start": v(20.65, -25.75) * mm, "end": v(23.84, -29.6) * mm});
            skLineSegment(sketch, "E9.6.61.0", {"start": v(21.03, -25.43) * mm, "end": v(22.63, -27.35) * mm});
            skPoint(sketch, "E9.9.61.0", {"position": v(22.63, -27.35) * mm});
            skLineSegment(sketch, "E9.10.61.0", {"start": v(23.84, -29.6) * mm, "end": v(24.6, -28.96) * mm});
            skLineSegment(sketch, "E9.13.61.0", {"start": v(20.65, -25.75) * mm, "end": v(21.42, -25.1) * mm});
            skLineSegment(sketch, "E9.1.62.0", {"start": v(22.95, -23.71) * mm, "end": v(26.38, -27.36) * mm});
            skLineSegment(sketch, "E9.3.62.0", {"start": v(22.23, -24.4) * mm, "end": v(25.65, -28.04) * mm});
            skLineSegment(sketch, "E9.6.62.0", {"start": v(22.6, -24.06) * mm, "end": v(24.3, -25.88) * mm});
            skPoint(sketch, "E9.9.62.0", {"position": v(24.3, -25.88) * mm});
            skLineSegment(sketch, "E9.10.62.0", {"start": v(25.65, -28.04) * mm, "end": v(26.38, -27.36) * mm});
            skLineSegment(sketch, "E9.13.62.0", {"start": v(22.23, -24.4) * mm, "end": v(22.95, -23.71) * mm});
            skLineSegment(sketch, "E9.1.63.0", {"start": v(24.4, -22.23) * mm, "end": v(28.04, -25.65) * mm});
            skLineSegment(sketch, "E9.3.63.0", {"start": v(23.71, -22.95) * mm, "end": v(27.36, -26.38) * mm});
            skLineSegment(sketch, "E9.6.63.0", {"start": v(24.06, -22.6) * mm, "end": v(25.88, -24.3) * mm});
            skPoint(sketch, "E9.9.63.0", {"position": v(25.88, -24.3) * mm});
            skLineSegment(sketch, "E9.10.63.0", {"start": v(27.36, -26.38) * mm, "end": v(28.04, -25.65) * mm});
            skLineSegment(sketch, "E9.13.63.0", {"start": v(23.71, -22.95) * mm, "end": v(24.4, -22.23) * mm});
            skLineSegment(sketch, "E9.1.64.0", {"start": v(25.75, -20.65) * mm, "end": v(29.6, -23.84) * mm});
            skLineSegment(sketch, "E9.3.64.0", {"start": v(25.1, -21.42) * mm, "end": v(28.96, -24.6) * mm});
            skLineSegment(sketch, "E9.6.64.0", {"start": v(25.43, -21.03) * mm, "end": v(27.35, -22.63) * mm});
            skPoint(sketch, "E9.9.64.0", {"position": v(27.35, -22.63) * mm});
            skLineSegment(sketch, "E9.10.64.0", {"start": v(28.96, -24.6) * mm, "end": v(29.6, -23.84) * mm});
            skLineSegment(sketch, "E9.13.64.0", {"start": v(25.1, -21.42) * mm, "end": v(25.75, -20.65) * mm});
            skLineSegment(sketch, "E9.1.65.0", {"start": v(27, -19) * mm, "end": v(31.04, -21.93) * mm});
            skLineSegment(sketch, "E9.3.65.0", {"start": v(26.4, -19.8) * mm, "end": v(30.45, -22.74) * mm});
            skLineSegment(sketch, "E9.6.65.0", {"start": v(26.7, -19.4) * mm, "end": v(28.72, -20.87) * mm});
            skPoint(sketch, "E9.9.65.0", {"position": v(28.72, -20.87) * mm});
            skLineSegment(sketch, "E9.10.65.0", {"start": v(30.45, -22.74) * mm, "end": v(31.04, -21.93) * mm});
            skLineSegment(sketch, "E9.13.65.0", {"start": v(26.4, -19.8) * mm, "end": v(27, -19) * mm});
            skLineSegment(sketch, "E9.1.66.0", {"start": v(28.13, -17.26) * mm, "end": v(32.35, -19.94) * mm});
            skLineSegment(sketch, "E9.3.66.0", {"start": v(27.6, -18.1) * mm, "end": v(31.82, -20.78) * mm});
            skLineSegment(sketch, "E9.6.66.0", {"start": v(27.86, -17.68) * mm, "end": v(29.97, -19.02) * mm});
            skPoint(sketch, "E9.9.66.0", {"position": v(29.97, -19.02) * mm});
            skLineSegment(sketch, "E9.10.66.0", {"start": v(31.82, -20.78) * mm, "end": v(32.35, -19.94) * mm});
            skLineSegment(sketch, "E9.13.66.0", {"start": v(27.6, -18.1) * mm, "end": v(28.13, -17.26) * mm});
            skLineSegment(sketch, "E9.1.67.0", {"start": v(29.16, -15.46) * mm, "end": v(33.54, -17.87) * mm});
            skLineSegment(sketch, "E9.3.67.0", {"start": v(28.68, -16.34) * mm, "end": v(33.06, -18.74) * mm});
            skLineSegment(sketch, "E9.6.67.0", {"start": v(28.92, -15.9) * mm, "end": v(31.1, -17.1) * mm});
            skPoint(sketch, "E9.9.67.0", {"position": v(31.1, -17.1) * mm});
            skLineSegment(sketch, "E9.10.67.0", {"start": v(33.06, -18.74) * mm, "end": v(33.54, -17.87) * mm});
            skLineSegment(sketch, "E9.13.67.0", {"start": v(28.68, -16.34) * mm, "end": v(29.16, -15.46) * mm});
            skLineSegment(sketch, "E9.1.68.0", {"start": v(30.07, -13.6) * mm, "end": v(34.6, -15.73) * mm});
            skLineSegment(sketch, "E9.3.68.0", {"start": v(29.65, -14.5) * mm, "end": v(34.17, -16.63) * mm});
            skLineSegment(sketch, "E9.6.68.0", {"start": v(29.86, -14.05) * mm, "end": v(32.12, -15.12) * mm});
            skPoint(sketch, "E9.9.68.0", {"position": v(32.12, -15.12) * mm});
            skLineSegment(sketch, "E9.10.68.0", {"start": v(34.17, -16.63) * mm, "end": v(34.6, -15.73) * mm});
            skLineSegment(sketch, "E9.13.68.0", {"start": v(29.65, -14.5) * mm, "end": v(30.07, -13.6) * mm});
            skLineSegment(sketch, "E9.1.69.0", {"start": v(30.87, -11.68) * mm, "end": v(35.52, -13.52) * mm});
            skLineSegment(sketch, "E9.3.69.0", {"start": v(30.5, -12.61) * mm, "end": v(35.15, -14.45) * mm});
            skLineSegment(sketch, "E9.6.69.0", {"start": v(30.68, -12.15) * mm, "end": v(33, -13.07) * mm});
            skPoint(sketch, "E9.9.69.0", {"position": v(33, -13.07) * mm});
            skLineSegment(sketch, "E9.10.69.0", {"start": v(35.15, -14.45) * mm, "end": v(35.52, -13.52) * mm});
            skLineSegment(sketch, "E9.13.69.0", {"start": v(30.5, -12.61) * mm, "end": v(30.87, -11.68) * mm});
            skLineSegment(sketch, "E10.1.70.0", {"start": v(31.54, -9.72) * mm, "end": v(36.3, -11.27) * mm});
            skLineSegment(sketch, "E10.3.70.0", {"start": v(31.23, -10.67) * mm, "end": v(35.99, -12.22) * mm});
            skLineSegment(sketch, "E10.6.70.0", {"start": v(31.38, -10.2) * mm, "end": v(33.76, -10.97) * mm});
            skPoint(sketch, "E10.9.70.0", {"position": v(33.76, -10.97) * mm});
            skLineSegment(sketch, "E10.10.70.0", {"start": v(35.99, -12.22) * mm, "end": v(36.3, -11.27) * mm});
            skLineSegment(sketch, "E10.13.70.0", {"start": v(31.23, -10.67) * mm, "end": v(31.54, -9.72) * mm});
            skLineSegment(sketch, "E10.1.71.0", {"start": v(32.09, -7.72) * mm, "end": v(36.93, -8.97) * mm});
            skLineSegment(sketch, "E10.3.71.0", {"start": v(31.84, -8.7) * mm, "end": v(36.68, -9.93) * mm});
            skLineSegment(sketch, "E10.6.71.0", {"start": v(31.96, -8.2) * mm, "end": v(34.38, -8.83) * mm});
            skPoint(sketch, "E10.9.71.0", {"position": v(34.38, -8.83) * mm});
            skLineSegment(sketch, "E10.10.71.0", {"start": v(36.68, -9.93) * mm, "end": v(36.93, -8.97) * mm});
            skLineSegment(sketch, "E10.13.71.0", {"start": v(31.84, -8.7) * mm, "end": v(32.09, -7.72) * mm});
            skLineSegment(sketch, "E10.1.72.0", {"start": v(32.5, -5.7) * mm, "end": v(37.42, -6.63) * mm});
            skLineSegment(sketch, "E10.3.72.0", {"start": v(32.32, -6.67) * mm, "end": v(37.23, -7.61) * mm});
            skLineSegment(sketch, "E10.6.72.0", {"start": v(32.42, -6.18) * mm, "end": v(34.87, -6.65) * mm});
            skPoint(sketch, "E10.9.72.0", {"position": v(34.87, -6.65) * mm});
            skLineSegment(sketch, "E10.10.72.0", {"start": v(37.23, -7.61) * mm, "end": v(37.42, -6.63) * mm});
            skLineSegment(sketch, "E10.13.72.0", {"start": v(32.32, -6.67) * mm, "end": v(32.5, -5.7) * mm});
            skLineSegment(sketch, "E10.1.73.0", {"start": v(32.8, -3.64) * mm, "end": v(37.76, -4.27) * mm});
            skLineSegment(sketch, "E10.3.73.0", {"start": v(32.68, -4.63) * mm, "end": v(37.64, -5.26) * mm});
            skLineSegment(sketch, "E10.6.73.0", {"start": v(32.74, -4.14) * mm, "end": v(35.22, -4.45) * mm});
            skPoint(sketch, "E10.9.73.0", {"position": v(35.22, -4.45) * mm});
            skLineSegment(sketch, "E10.10.73.0", {"start": v(37.64, -5.26) * mm, "end": v(37.76, -4.27) * mm});
            skLineSegment(sketch, "E10.13.73.0", {"start": v(32.68, -4.63) * mm, "end": v(32.8, -3.64) * mm});
            skLineSegment(sketch, "E10.1.74.0", {"start": v(32.97, -1.57) * mm, "end": v(37.96, -1.89) * mm});
            skLineSegment(sketch, "E10.3.74.0", {"start": v(32.9, -2.57) * mm, "end": v(37.9, -2.89) * mm});
            skLineSegment(sketch, "E10.6.74.0", {"start": v(32.93, -2.07) * mm, "end": v(35.43, -2.23) * mm});
            skPoint(sketch, "E10.9.74.0", {"position": v(35.43, -2.23) * mm});
            skLineSegment(sketch, "E10.10.74.0", {"start": v(37.9, -2.89) * mm, "end": v(37.96, -1.89) * mm});
            skLineSegment(sketch, "E10.13.74.0", {"start": v(32.9, -2.57) * mm, "end": v(32.97, -1.57) * mm});
            skLineSegment(sketch, "E10.1.75.0", {"start": v(33, 0.5) * mm, "end": v(38, 0.5) * mm});
            skLineSegment(sketch, "E10.3.75.0", {"start": v(33, -0.5) * mm, "end": v(38, -0.5) * mm});
            skLineSegment(sketch, "E10.6.75.0", {"start": v(33, 0) * mm, "end": v(35.5, 0) * mm});
            skPoint(sketch, "E10.9.75.0", {"position": v(35.5, 0) * mm});
            skLineSegment(sketch, "E10.10.75.0", {"start": v(38, -0.5) * mm, "end": v(38, 0.5) * mm});
            skLineSegment(sketch, "E10.13.75.0", {"start": v(33, -0.5) * mm, "end": v(33, 0.5) * mm});
            skLineSegment(sketch, "E10.1.76.0", {"start": v(32.9, 2.57) * mm, "end": v(37.9, 2.89) * mm});
            skLineSegment(sketch, "E10.3.76.0", {"start": v(32.97, 1.57) * mm, "end": v(37.96, 1.89) * mm});
            skLineSegment(sketch, "E10.6.76.0", {"start": v(32.93, 2.07) * mm, "end": v(35.43, 2.23) * mm});
            skPoint(sketch, "E10.9.76.0", {"position": v(35.43, 2.23) * mm});
            skLineSegment(sketch, "E10.10.76.0", {"start": v(37.96, 1.89) * mm, "end": v(37.9, 2.89) * mm});
            skLineSegment(sketch, "E10.13.76.0", {"start": v(32.97, 1.57) * mm, "end": v(32.9, 2.57) * mm});
            skLineSegment(sketch, "E10.1.77.0", {"start": v(32.68, 4.63) * mm, "end": v(37.64, 5.26) * mm});
            skLineSegment(sketch, "E10.3.77.0", {"start": v(32.8, 3.64) * mm, "end": v(37.76, 4.27) * mm});
            skLineSegment(sketch, "E10.6.77.0", {"start": v(32.74, 4.14) * mm, "end": v(35.22, 4.45) * mm});
            skPoint(sketch, "E10.9.77.0", {"position": v(35.22, 4.45) * mm});
            skLineSegment(sketch, "E10.10.77.0", {"start": v(37.76, 4.27) * mm, "end": v(37.64, 5.26) * mm});
            skLineSegment(sketch, "E10.13.77.0", {"start": v(32.8, 3.64) * mm, "end": v(32.68, 4.63) * mm});
            skLineSegment(sketch, "E10.1.78.0", {"start": v(32.32, 6.67) * mm, "end": v(37.23, 7.61) * mm});
            skLineSegment(sketch, "E10.3.78.0", {"start": v(32.5, 5.7) * mm, "end": v(37.42, 6.63) * mm});
            skLineSegment(sketch, "E10.6.78.0", {"start": v(32.42, 6.18) * mm, "end": v(34.87, 6.65) * mm});
            skPoint(sketch, "E10.9.78.0", {"position": v(34.87, 6.65) * mm});
            skLineSegment(sketch, "E10.10.78.0", {"start": v(37.42, 6.63) * mm, "end": v(37.23, 7.61) * mm});
            skLineSegment(sketch, "E10.13.78.0", {"start": v(32.5, 5.7) * mm, "end": v(32.32, 6.67) * mm});
            skLineSegment(sketch, "E10.1.79.0", {"start": v(31.84, 8.7) * mm, "end": v(36.68, 9.93) * mm});
            skLineSegment(sketch, "E10.3.79.0", {"start": v(32.09, 7.72) * mm, "end": v(36.93, 8.97) * mm});
            skLineSegment(sketch, "E10.6.79.0", {"start": v(31.96, 8.2) * mm, "end": v(34.38, 8.83) * mm});
            skPoint(sketch, "E10.9.79.0", {"position": v(34.38, 8.83) * mm});
            skLineSegment(sketch, "E10.10.79.0", {"start": v(36.93, 8.97) * mm, "end": v(36.68, 9.93) * mm});
            skLineSegment(sketch, "E10.13.79.0", {"start": v(32.09, 7.72) * mm, "end": v(31.84, 8.7) * mm});
            skLineSegment(sketch, "E10.1.80.0", {"start": v(31.23, 10.67) * mm, "end": v(35.99, 12.22) * mm});
            skLineSegment(sketch, "E10.3.80.0", {"start": v(31.54, 9.72) * mm, "end": v(36.3, 11.27) * mm});
            skLineSegment(sketch, "E10.6.80.0", {"start": v(31.38, 10.2) * mm, "end": v(33.76, 10.97) * mm});
            skPoint(sketch, "E10.9.80.0", {"position": v(33.76, 10.97) * mm});
            skLineSegment(sketch, "E10.10.80.0", {"start": v(36.3, 11.27) * mm, "end": v(35.99, 12.22) * mm});
            skLineSegment(sketch, "E10.13.80.0", {"start": v(31.54, 9.72) * mm, "end": v(31.23, 10.67) * mm});
            skLineSegment(sketch, "E10.1.81.0", {"start": v(30.5, 12.61) * mm, "end": v(35.15, 14.45) * mm});
            skLineSegment(sketch, "E10.3.81.0", {"start": v(30.87, 11.68) * mm, "end": v(35.52, 13.52) * mm});
            skLineSegment(sketch, "E10.6.81.0", {"start": v(30.68, 12.15) * mm, "end": v(33, 13.07) * mm});
            skPoint(sketch, "E10.9.81.0", {"position": v(33, 13.07) * mm});
            skLineSegment(sketch, "E10.10.81.0", {"start": v(35.52, 13.52) * mm, "end": v(35.15, 14.45) * mm});
            skLineSegment(sketch, "E10.13.81.0", {"start": v(30.87, 11.68) * mm, "end": v(30.5, 12.61) * mm});
            skLineSegment(sketch, "E10.1.82.0", {"start": v(29.65, 14.5) * mm, "end": v(34.17, 16.63) * mm});
            skLineSegment(sketch, "E10.3.82.0", {"start": v(30.07, 13.6) * mm, "end": v(34.6, 15.73) * mm});
            skLineSegment(sketch, "E10.6.82.0", {"start": v(29.86, 14.05) * mm, "end": v(32.12, 15.12) * mm});
            skPoint(sketch, "E10.9.82.0", {"position": v(32.12, 15.12) * mm});
            skLineSegment(sketch, "E10.10.82.0", {"start": v(34.6, 15.73) * mm, "end": v(34.17, 16.63) * mm});
            skLineSegment(sketch, "E10.13.82.0", {"start": v(30.07, 13.6) * mm, "end": v(29.65, 14.5) * mm});
            skLineSegment(sketch, "E10.1.83.0", {"start": v(28.68, 16.34) * mm, "end": v(33.06, 18.74) * mm});
            skLineSegment(sketch, "E10.3.83.0", {"start": v(29.16, 15.46) * mm, "end": v(33.54, 17.87) * mm});
            skLineSegment(sketch, "E10.6.83.0", {"start": v(28.92, 15.9) * mm, "end": v(31.1, 17.1) * mm});
            skPoint(sketch, "E10.9.83.0", {"position": v(31.1, 17.1) * mm});
            skLineSegment(sketch, "E10.10.83.0", {"start": v(33.54, 17.87) * mm, "end": v(33.06, 18.74) * mm});
            skLineSegment(sketch, "E10.13.83.0", {"start": v(29.16, 15.46) * mm, "end": v(28.68, 16.34) * mm});
            skLineSegment(sketch, "E10.1.84.0", {"start": v(27.6, 18.1) * mm, "end": v(31.82, 20.78) * mm});
            skLineSegment(sketch, "E10.3.84.0", {"start": v(28.13, 17.26) * mm, "end": v(32.35, 19.94) * mm});
            skLineSegment(sketch, "E10.6.84.0", {"start": v(27.86, 17.68) * mm, "end": v(29.97, 19.02) * mm});
            skPoint(sketch, "E10.9.84.0", {"position": v(29.97, 19.02) * mm});
            skLineSegment(sketch, "E10.10.84.0", {"start": v(32.35, 19.94) * mm, "end": v(31.82, 20.78) * mm});
            skLineSegment(sketch, "E10.13.84.0", {"start": v(28.13, 17.26) * mm, "end": v(27.6, 18.1) * mm});
            skLineSegment(sketch, "E10.1.85.0", {"start": v(26.4, 19.8) * mm, "end": v(30.45, 22.74) * mm});
            skLineSegment(sketch, "E10.3.85.0", {"start": v(27, 19) * mm, "end": v(31.04, 21.93) * mm});
            skLineSegment(sketch, "E10.6.85.0", {"start": v(26.7, 19.4) * mm, "end": v(28.72, 20.87) * mm});
            skPoint(sketch, "E10.9.85.0", {"position": v(28.72, 20.87) * mm});
            skLineSegment(sketch, "E10.10.85.0", {"start": v(31.04, 21.93) * mm, "end": v(30.45, 22.74) * mm});
            skLineSegment(sketch, "E10.13.85.0", {"start": v(27, 19) * mm, "end": v(26.4, 19.8) * mm});
            skLineSegment(sketch, "E10.1.86.0", {"start": v(25.1, 21.42) * mm, "end": v(28.96, 24.6) * mm});
            skLineSegment(sketch, "E10.3.86.0", {"start": v(25.75, 20.65) * mm, "end": v(29.6, 23.84) * mm});
            skLineSegment(sketch, "E10.6.86.0", {"start": v(25.43, 21.03) * mm, "end": v(27.35, 22.63) * mm});
            skPoint(sketch, "E10.9.86.0", {"position": v(27.35, 22.63) * mm});
            skLineSegment(sketch, "E10.10.86.0", {"start": v(29.6, 23.84) * mm, "end": v(28.96, 24.6) * mm});
            skLineSegment(sketch, "E10.13.86.0", {"start": v(25.75, 20.65) * mm, "end": v(25.1, 21.42) * mm});
            skLineSegment(sketch, "E10.1.87.0", {"start": v(23.71, 22.95) * mm, "end": v(27.36, 26.38) * mm});
            skLineSegment(sketch, "E10.3.87.0", {"start": v(24.4, 22.23) * mm, "end": v(28.04, 25.65) * mm});
            skLineSegment(sketch, "E10.6.87.0", {"start": v(24.06, 22.6) * mm, "end": v(25.88, 24.3) * mm});
            skPoint(sketch, "E10.9.87.0", {"position": v(25.88, 24.3) * mm});
            skLineSegment(sketch, "E10.10.87.0", {"start": v(28.04, 25.65) * mm, "end": v(27.36, 26.38) * mm});
            skLineSegment(sketch, "E10.13.87.0", {"start": v(24.4, 22.23) * mm, "end": v(23.71, 22.95) * mm});
            skLineSegment(sketch, "E10.1.88.0", {"start": v(22.23, 24.4) * mm, "end": v(25.65, 28.04) * mm});
            skLineSegment(sketch, "E10.3.88.0", {"start": v(22.95, 23.71) * mm, "end": v(26.38, 27.36) * mm});
            skLineSegment(sketch, "E10.6.88.0", {"start": v(22.6, 24.06) * mm, "end": v(24.3, 25.88) * mm});
            skPoint(sketch, "E10.9.88.0", {"position": v(24.3, 25.88) * mm});
            skLineSegment(sketch, "E10.10.88.0", {"start": v(26.38, 27.36) * mm, "end": v(25.65, 28.04) * mm});
            skLineSegment(sketch, "E10.13.88.0", {"start": v(22.95, 23.71) * mm, "end": v(22.23, 24.4) * mm});
            skLineSegment(sketch, "E10.1.89.0", {"start": v(20.65, 25.75) * mm, "end": v(23.84, 29.6) * mm});
            skLineSegment(sketch, "E10.3.89.0", {"start": v(21.42, 25.1) * mm, "end": v(24.6, 28.96) * mm});
            skLineSegment(sketch, "E10.6.89.0", {"start": v(21.03, 25.43) * mm, "end": v(22.63, 27.35) * mm});
            skPoint(sketch, "E10.9.89.0", {"position": v(22.63, 27.35) * mm});
            skLineSegment(sketch, "E10.10.89.0", {"start": v(24.6, 28.96) * mm, "end": v(23.84, 29.6) * mm});
            skLineSegment(sketch, "E10.13.89.0", {"start": v(21.42, 25.1) * mm, "end": v(20.65, 25.75) * mm});
            skLineSegment(sketch, "E10.1.90.0", {"start": v(19, 27) * mm, "end": v(21.93, 31.04) * mm});
            skLineSegment(sketch, "E10.3.90.0", {"start": v(19.8, 26.4) * mm, "end": v(22.74, 30.45) * mm});
            skLineSegment(sketch, "E10.6.90.0", {"start": v(19.4, 26.7) * mm, "end": v(20.87, 28.72) * mm});
            skPoint(sketch, "E10.9.90.0", {"position": v(20.87, 28.72) * mm});
            skLineSegment(sketch, "E10.10.90.0", {"start": v(22.74, 30.45) * mm, "end": v(21.93, 31.04) * mm});
            skLineSegment(sketch, "E10.13.90.0", {"start": v(19.8, 26.4) * mm, "end": v(19, 27) * mm});
            skLineSegment(sketch, "E10.1.91.0", {"start": v(17.26, 28.13) * mm, "end": v(19.94, 32.35) * mm});
            skLineSegment(sketch, "E10.3.91.0", {"start": v(18.1, 27.6) * mm, "end": v(20.78, 31.82) * mm});
            skLineSegment(sketch, "E10.6.91.0", {"start": v(17.68, 27.86) * mm, "end": v(19.02, 29.97) * mm});
            skPoint(sketch, "E10.9.91.0", {"position": v(19.02, 29.97) * mm});
            skLineSegment(sketch, "E10.10.91.0", {"start": v(20.78, 31.82) * mm, "end": v(19.94, 32.35) * mm});
            skLineSegment(sketch, "E10.13.91.0", {"start": v(18.1, 27.6) * mm, "end": v(17.26, 28.13) * mm});
            skLineSegment(sketch, "E10.1.92.0", {"start": v(15.46, 29.16) * mm, "end": v(17.87, 33.54) * mm});
            skLineSegment(sketch, "E10.3.92.0", {"start": v(16.34, 28.68) * mm, "end": v(18.74, 33.06) * mm});
            skLineSegment(sketch, "E10.6.92.0", {"start": v(15.9, 28.92) * mm, "end": v(17.1, 31.1) * mm});
            skPoint(sketch, "E10.9.92.0", {"position": v(17.1, 31.1) * mm});
            skLineSegment(sketch, "E10.10.92.0", {"start": v(18.74, 33.06) * mm, "end": v(17.87, 33.54) * mm});
            skLineSegment(sketch, "E10.13.92.0", {"start": v(16.34, 28.68) * mm, "end": v(15.46, 29.16) * mm});
            skLineSegment(sketch, "E10.1.93.0", {"start": v(13.6, 30.07) * mm, "end": v(15.73, 34.6) * mm});
            skLineSegment(sketch, "E10.3.93.0", {"start": v(14.5, 29.65) * mm, "end": v(16.63, 34.17) * mm});
            skLineSegment(sketch, "E10.6.93.0", {"start": v(14.05, 29.86) * mm, "end": v(15.12, 32.12) * mm});
            skPoint(sketch, "E10.9.93.0", {"position": v(15.12, 32.12) * mm});
            skLineSegment(sketch, "E10.10.93.0", {"start": v(16.63, 34.17) * mm, "end": v(15.73, 34.6) * mm});
            skLineSegment(sketch, "E10.13.93.0", {"start": v(14.5, 29.65) * mm, "end": v(13.6, 30.07) * mm});
            skLineSegment(sketch, "E10.1.94.0", {"start": v(11.68, 30.87) * mm, "end": v(13.52, 35.52) * mm});
            skLineSegment(sketch, "E10.3.94.0", {"start": v(12.61, 30.5) * mm, "end": v(14.45, 35.15) * mm});
            skLineSegment(sketch, "E10.6.94.0", {"start": v(12.15, 30.68) * mm, "end": v(13.07, 33) * mm});
            skPoint(sketch, "E10.9.94.0", {"position": v(13.07, 33) * mm});
            skLineSegment(sketch, "E10.10.94.0", {"start": v(14.45, 35.15) * mm, "end": v(13.52, 35.52) * mm});
            skLineSegment(sketch, "E10.13.94.0", {"start": v(12.61, 30.5) * mm, "end": v(11.68, 30.87) * mm});
            skLineSegment(sketch, "E10.1.95.0", {"start": v(9.72, 31.54) * mm, "end": v(11.27, 36.3) * mm});
            skLineSegment(sketch, "E10.3.95.0", {"start": v(10.67, 31.23) * mm, "end": v(12.22, 35.99) * mm});
            skLineSegment(sketch, "E10.6.95.0", {"start": v(10.2, 31.38) * mm, "end": v(10.97, 33.76) * mm});
            skPoint(sketch, "E10.9.95.0", {"position": v(10.97, 33.76) * mm});
            skLineSegment(sketch, "E10.10.95.0", {"start": v(12.22, 35.99) * mm, "end": v(11.27, 36.3) * mm});
            skLineSegment(sketch, "E10.13.95.0", {"start": v(10.67, 31.23) * mm, "end": v(9.72, 31.54) * mm});
            skLineSegment(sketch, "E10.1.96.0", {"start": v(7.72, 32.09) * mm, "end": v(8.97, 36.93) * mm});
            skLineSegment(sketch, "E10.3.96.0", {"start": v(8.7, 31.84) * mm, "end": v(9.93, 36.68) * mm});
            skLineSegment(sketch, "E10.6.96.0", {"start": v(8.2, 31.96) * mm, "end": v(8.83, 34.38) * mm});
            skPoint(sketch, "E10.9.96.0", {"position": v(8.83, 34.38) * mm});
            skLineSegment(sketch, "E10.10.96.0", {"start": v(9.93, 36.68) * mm, "end": v(8.97, 36.93) * mm});
            skLineSegment(sketch, "E10.13.96.0", {"start": v(8.7, 31.84) * mm, "end": v(7.72, 32.09) * mm});
            skLineSegment(sketch, "E10.1.97.0", {"start": v(5.7, 32.5) * mm, "end": v(6.63, 37.42) * mm});
            skLineSegment(sketch, "E10.3.97.0", {"start": v(6.67, 32.32) * mm, "end": v(7.61, 37.23) * mm});
            skLineSegment(sketch, "E10.6.97.0", {"start": v(6.18, 32.42) * mm, "end": v(6.65, 34.87) * mm});
            skPoint(sketch, "E10.9.97.0", {"position": v(6.65, 34.87) * mm});
            skLineSegment(sketch, "E10.10.97.0", {"start": v(7.61, 37.23) * mm, "end": v(6.63, 37.42) * mm});
            skLineSegment(sketch, "E10.13.97.0", {"start": v(6.67, 32.32) * mm, "end": v(5.7, 32.5) * mm});
            skLineSegment(sketch, "E10.1.98.0", {"start": v(3.64, 32.8) * mm, "end": v(4.27, 37.76) * mm});
            skLineSegment(sketch, "E10.3.98.0", {"start": v(4.63, 32.68) * mm, "end": v(5.26, 37.64) * mm});
            skLineSegment(sketch, "E10.6.98.0", {"start": v(4.14, 32.74) * mm, "end": v(4.45, 35.22) * mm});
            skPoint(sketch, "E10.9.98.0", {"position": v(4.45, 35.22) * mm});
            skLineSegment(sketch, "E10.10.98.0", {"start": v(5.26, 37.64) * mm, "end": v(4.27, 37.76) * mm});
            skLineSegment(sketch, "E10.13.98.0", {"start": v(4.63, 32.68) * mm, "end": v(3.64, 32.8) * mm});
            skLineSegment(sketch, "E10.1.99.0", {"start": v(1.57, 32.97) * mm, "end": v(1.89, 37.96) * mm});
            skLineSegment(sketch, "E10.3.99.0", {"start": v(2.57, 32.9) * mm, "end": v(2.89, 37.9) * mm});
            skLineSegment(sketch, "E10.6.99.0", {"start": v(2.07, 32.93) * mm, "end": v(2.23, 35.43) * mm});
            skPoint(sketch, "E10.9.99.0", {"position": v(2.23, 35.43) * mm});
            skLineSegment(sketch, "E10.10.99.0", {"start": v(2.89, 37.9) * mm, "end": v(1.89, 37.96) * mm});
            skLineSegment(sketch, "E10.13.99.0", {"start": v(2.57, 32.9) * mm, "end": v(1.57, 32.97) * mm});
            skSolve(sketch);
        }
        {
            var Q0;
            Q0=makeQuery(id+"F0.imprint","IMPRINT",FACE,{"disambiguationData":[TD([[makeQuery(id+"F0.imprint","IMPRINT",EDGE,{"derivedFrom":sQuery(id+"F0.wireOp",EDGE,"E0")}),1.0]])]});
            extrude(context, id + "F1", {"entities" : qUnion([Q0]), "depth" : 3 * mm});
        }
    });
